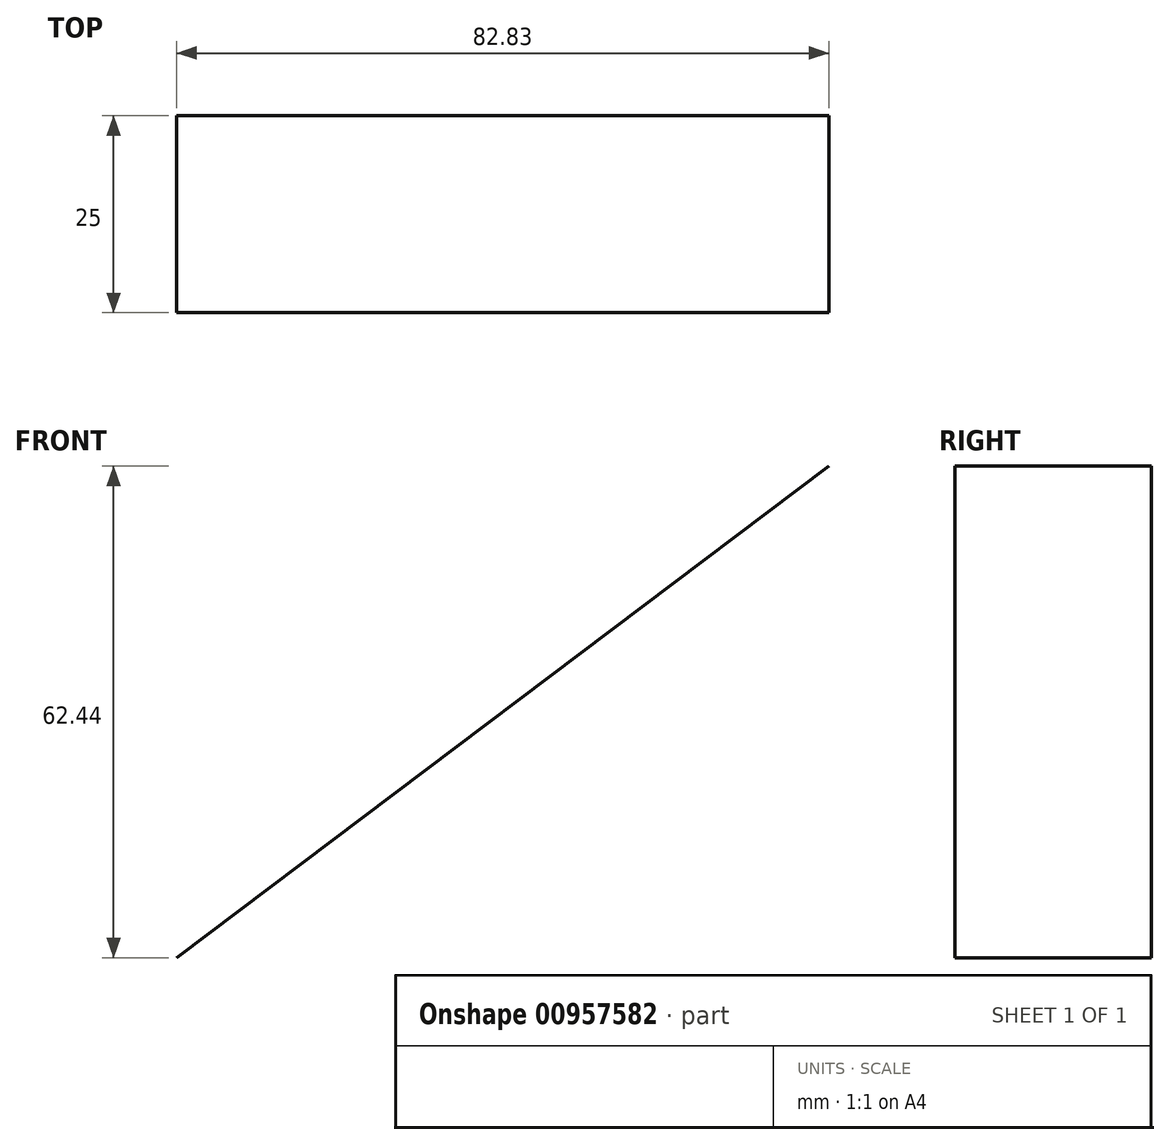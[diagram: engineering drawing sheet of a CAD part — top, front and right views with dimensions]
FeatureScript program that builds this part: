
annotation { "Feature Type Name" : "Feature", "Feature Type Description" : "" }
export const myFeature = defineFeature(function(context is Context, id is Id, definition is map)
    precondition{}
    {
        {
            var Q0;
            Q0=qCreatedBy(makeId("Front.planeOp"),FACE);
            var sketch = newSketch(context, id + "F0", { "sketchPlane" : qUnion([Q0])});
            skLineSegment(sketch, "E0", {"start": v(0, 39.6) * mm, "end": v(82.83, 102.04) * mm});
            skSolve(sketch);
        }
        {
            var Q0;
            Q0=sQuery(id+"F0.wireOp",EDGE,"E0");
            extrude(context, id + "F1", {"bodyType" : ToolBodyType.SURFACE, "surfaceEntities" : qUnion([Q0]), "depth" : 25 * mm, "offsetDistance" : 25 * mm});
        }
    });
